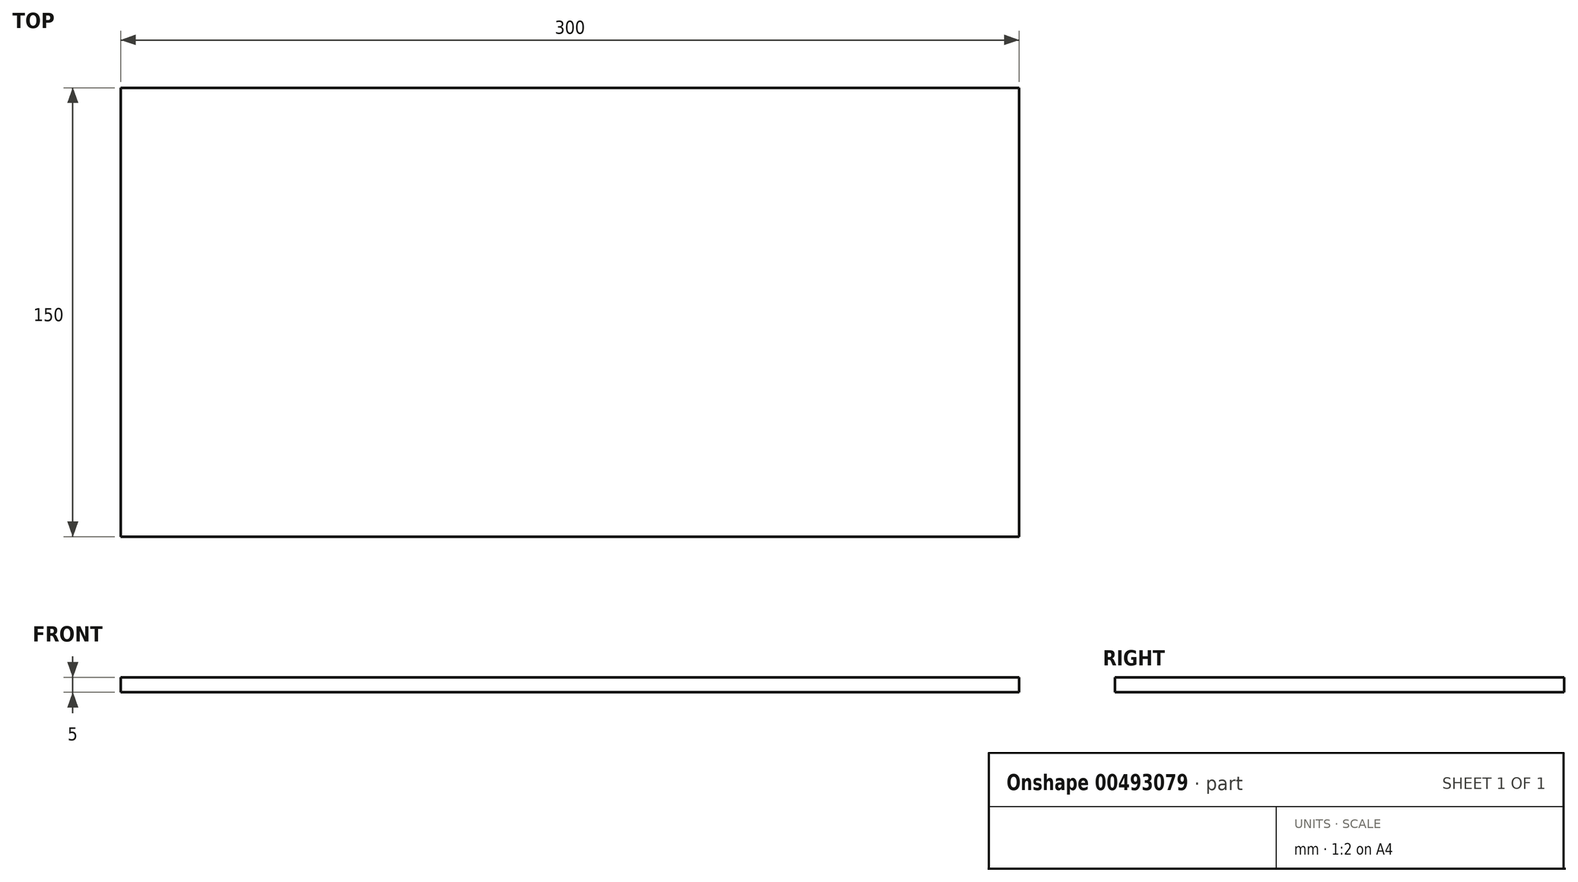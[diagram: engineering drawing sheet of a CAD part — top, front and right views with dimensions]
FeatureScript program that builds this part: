
annotation { "Feature Type Name" : "Feature", "Feature Type Description" : "" }
export const myFeature = defineFeature(function(context is Context, id is Id, definition is map)
    precondition{}
    {
        {
            var Q0;
            Q0=qCreatedBy(makeId("Top.planeOp"),FACE);
            var sketch = newSketch(context, id + "F0", { "sketchPlane" : qUnion([Q0])});
            skLineSegment(sketch, "E0.bottom", {"start": v(-150, 75) * mm, "end": v(150, 75) * mm});
            skLineSegment(sketch, "E0.top", {"start": v(-150, -75) * mm, "end": v(150, -75) * mm});
            skLineSegment(sketch, "E0.left", {"start": v(-150, 75) * mm, "end": v(-150, -75) * mm});
            skLineSegment(sketch, "E0.right", {"start": v(150, 75) * mm, "end": v(150, -75) * mm});
            skSolve(sketch);
        }
        {
            var Q0;
            Q0=makeQuery(id+"F0.imprint","IMPRINT",FACE,{"disambiguationData":[TD([[makeQuery(id+"F0.imprint","IMPRINT",EDGE,{"derivedFrom":sQuery(id+"F0.wireOp",EDGE,"E0.bottom")}),-1.0]])]});
            extrude(context, id + "F1", {"entities" : qUnion([Q0]), "depth" : 5 * mm});
        }
    });
